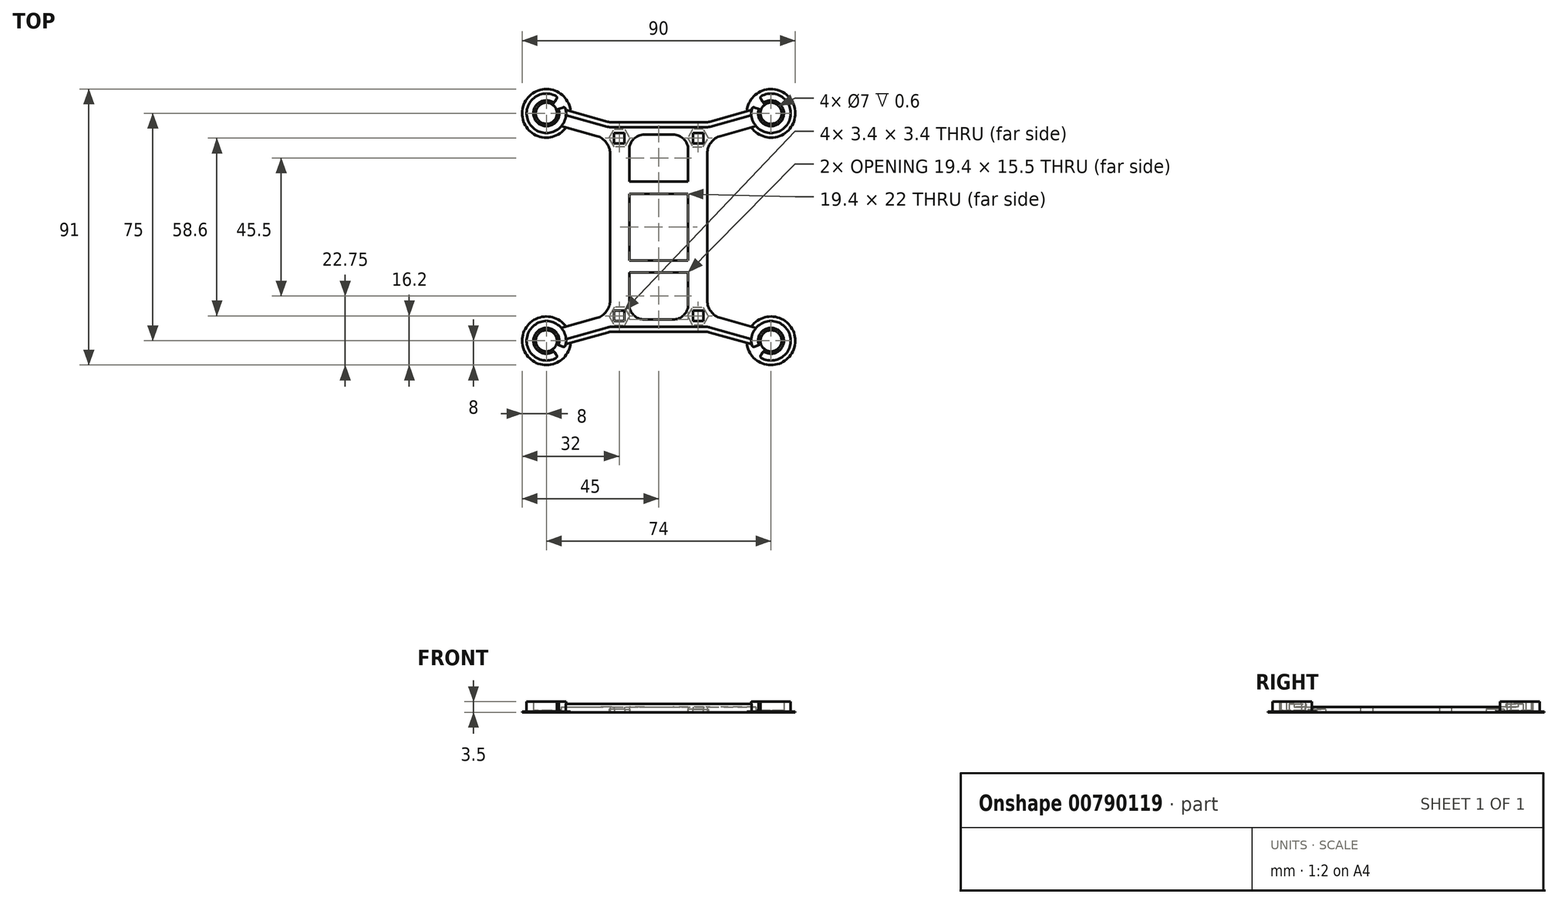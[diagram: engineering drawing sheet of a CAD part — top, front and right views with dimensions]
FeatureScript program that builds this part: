
annotation { "Feature Type Name" : "Feature", "Feature Type Description" : "" }
export const myFeature = defineFeature(function(context is Context, id is Id, definition is map)
    precondition{}
    {
        {
            var Q0;
            Q0=qCreatedBy(makeId("Top.planeOp"),FACE);
            var sketch = newSketch(context, id + "F0", { "sketchPlane" : qUnion([Q0])});
            skCircle(sketch, "E0", {"center": v(-37, 37.5) * mm, "radius": 32.5 * mm, "construction": true});
            skCircle(sketch, "E1.MirrorC", {"center": v(37, 37.5) * mm, "radius": 32.5 * mm, "construction": true});
            skCircle(sketch, "E2.MirrorC", {"center": v(37, -37.5) * mm, "radius": 32.5 * mm, "construction": true});
            skCircle(sketch, "E3.MirrorC", {"center": v(-37, -37.5) * mm, "radius": 32.5 * mm, "construction": true});
            skLineSegment(sketch, "E4.bottom", {"start": v(-37, 37.5) * mm, "end": v(37, 37.5) * mm, "construction": true});
            skLineSegment(sketch, "E4.top", {"start": v(-37, -37.5) * mm, "end": v(37, -37.5) * mm, "construction": true});
            skLineSegment(sketch, "E4.left", {"start": v(-37, 37.5) * mm, "end": v(-37, -37.5) * mm, "construction": true});
            skLineSegment(sketch, "E4.right", {"start": v(37, 37.5) * mm, "end": v(37, -37.5) * mm, "construction": true});
            skLineSegment(sketch, "E5", {"start": v(-37, 37.5) * mm, "end": v(0, 0) * mm, "construction": true});
            skCircle(sketch, "E6", {"center": v(-37, 37.5) * mm, "radius": 3.5 * mm});
            skCircle(sketch, "E7.MirrorC", {"center": v(37, 37.5) * mm, "radius": 3.5 * mm});
            skCircle(sketch, "E8.MirrorC", {"center": v(37, -37.5) * mm, "radius": 3.5 * mm});
            skCircle(sketch, "E9.MirrorC", {"center": v(-37, -37.5) * mm, "radius": 3.5 * mm});
            skArc(sketch, "E10", {"start": v(-30.59, 38.57) * mm, "mid": v(-43.26, 39.25) * mm, "end": v(-32.07, 33.27) * mm});
            skArc(sketch, "E11.MirrorC", {"start": v(30.59, 38.57) * mm, "mid": v(43.26, 39.25) * mm, "end": v(32.07, 33.27) * mm});
            skArc(sketch, "E12.MirrorC", {"start": v(-30.59, -38.57) * mm, "mid": v(-43.26, -39.25) * mm, "end": v(-32.07, -33.27) * mm});
            skArc(sketch, "E13.MirrorC", {"start": v(30.59, -38.57) * mm, "mid": v(43.26, -39.25) * mm, "end": v(32.07, -33.27) * mm});
            skLineSegment(sketch, "E14.bottom", {"start": v(-16, 34.5) * mm, "end": v(16, 34.5) * mm});
            skLineSegment(sketch, "E14.top", {"start": v(-16, -34.5) * mm, "end": v(16, -34.5) * mm});
            skLineSegment(sketch, "E14.left", {"start": v(-16, 28.8) * mm, "end": v(-16, -28.8) * mm});
            skLineSegment(sketch, "E14.right", {"start": v(16, 28.8) * mm, "end": v(16, -28.8) * mm});
            skLineSegment(sketch, "E15", {"start": v(-30.59, 38.57) * mm, "end": v(-16, 34.5) * mm});
            skLineSegment(sketch, "E16", {"start": v(-32.07, 33.27) * mm, "end": v(-16, 28.8) * mm});
            skLineSegment(sketch, "E17", {"start": v(-37, 37.5) * mm, "end": v(-17.81, 32.15) * mm, "construction": true});
            skLineSegment(sketch, "E18.MirrorCS", {"start": v(30.59, 38.57) * mm, "end": v(16, 34.5) * mm});
            skLineSegment(sketch, "E19.MirrorCS", {"start": v(32.07, 33.27) * mm, "end": v(16, 28.8) * mm});
            skLineSegment(sketch, "E20.MirrorCS", {"start": v(-30.59, -38.57) * mm, "end": v(-16, -34.5) * mm});
            skLineSegment(sketch, "E21.MirrorCS", {"start": v(-32.07, -33.27) * mm, "end": v(-16, -28.8) * mm});
            skLineSegment(sketch, "E22.MirrorCS", {"start": v(30.59, -38.57) * mm, "end": v(16, -34.5) * mm});
            skLineSegment(sketch, "E23.MirrorCS", {"start": v(32.07, -33.27) * mm, "end": v(16, -28.8) * mm});
            skCircle(sketch, "E24", {"center": v(-13, 29.3) * mm, "radius": 1.7 * mm, "construction": true});
            skLineSegment(sketch, "E25.bottom", {"start": v(-14.7, 27.6) * mm, "end": v(-11.3, 27.6) * mm});
            skLineSegment(sketch, "E25.top", {"start": v(-14.7, 31) * mm, "end": v(-11.3, 31) * mm});
            skLineSegment(sketch, "E25.left", {"start": v(-14.7, 27.6) * mm, "end": v(-14.7, 31) * mm});
            skLineSegment(sketch, "E25.right", {"start": v(-11.3, 27.6) * mm, "end": v(-11.3, 31) * mm});
            skCircle(sketch, "E26.MirrorC", {"center": v(13, 29.3) * mm, "radius": 1.7 * mm, "construction": true});
            skLineSegment(sketch, "E27.MirrorCS", {"start": v(14.7, 27.6) * mm, "end": v(14.7, 31) * mm});
            skLineSegment(sketch, "E28.MirrorCS", {"start": v(14.7, 27.6) * mm, "end": v(11.3, 27.6) * mm});
            skLineSegment(sketch, "E29.MirrorCS", {"start": v(14.7, 31) * mm, "end": v(11.3, 31) * mm});
            skLineSegment(sketch, "E30.MirrorCS", {"start": v(11.3, 27.6) * mm, "end": v(11.3, 31) * mm});
            skLineSegment(sketch, "E31.MirrorCS", {"start": v(-11.3, -27.6) * mm, "end": v(-11.3, -31) * mm});
            skLineSegment(sketch, "E32.MirrorCS", {"start": v(-14.7, -27.6) * mm, "end": v(-11.3, -27.6) * mm});
            skPoint(sketch, "E33.MirrorP", {"position": v(-13, -29.3) * mm});
            skLineSegment(sketch, "E34.MirrorCS", {"start": v(-14.7, -27.6) * mm, "end": v(-14.7, -31) * mm});
            skLineSegment(sketch, "E35.MirrorCS", {"start": v(-14.7, -31) * mm, "end": v(-11.3, -31) * mm});
            skCircle(sketch, "E36.MirrorC", {"center": v(-13, -29.3) * mm, "radius": 1.7 * mm, "construction": true});
            skLineSegment(sketch, "E37.MirrorCS", {"start": v(11.3, -27.6) * mm, "end": v(11.3, -31) * mm});
            skLineSegment(sketch, "E38.MirrorCS", {"start": v(14.7, -27.6) * mm, "end": v(14.7, -31) * mm});
            skPoint(sketch, "E39.MirrorP", {"position": v(13, -29.3) * mm});
            skLineSegment(sketch, "E40.MirrorCS", {"start": v(14.7, -27.6) * mm, "end": v(11.3, -27.6) * mm});
            skLineSegment(sketch, "E41.MirrorCS", {"start": v(14.7, -31) * mm, "end": v(11.3, -31) * mm});
            skCircle(sketch, "E42.MirrorC", {"center": v(13, -29.3) * mm, "radius": 1.7 * mm, "construction": true});
            skLineSegment(sketch, "E43.bottom", {"start": v(-9.7, 30.5) * mm, "end": v(9.7, 30.5) * mm});
            skLineSegment(sketch, "E43.top", {"start": v(-9.7, -30.5) * mm, "end": v(9.7, -30.5) * mm});
            skLineSegment(sketch, "E43.left", {"start": v(-9.7, 30.5) * mm, "end": v(-9.7, 15) * mm});
            skLineSegment(sketch, "E43.right", {"start": v(9.7, 30.5) * mm, "end": v(9.7, 15) * mm});
            skPoint(sketch, "E43.middle", {"position": v(0, 0) * mm});
            skLineSegment(sketch, "E44", {"start": v(-9.7, 15) * mm, "end": v(9.7, 15) * mm});
            skLineSegment(sketch, "E45", {"start": v(-9.7, 11) * mm, "end": v(9.7, 11) * mm});
            skLineSegment(sketch, "E46.trimOffspring", {"start": v(-9.7, 11) * mm, "end": v(-9.7, -11) * mm});
            skLineSegment(sketch, "E47.trimOffspring", {"start": v(9.7, 11) * mm, "end": v(9.7, -11) * mm});
            skLineSegment(sketch, "E48.MirrorCS", {"start": v(-9.7, -15) * mm, "end": v(9.7, -15) * mm});
            skLineSegment(sketch, "E49.MirrorCS", {"start": v(-9.7, -11) * mm, "end": v(9.7, -11) * mm});
            skLineSegment(sketch, "E50.trimOffspring", {"start": v(-9.7, -15) * mm, "end": v(-9.7, -30.5) * mm});
            skLineSegment(sketch, "E51.trimOffspring", {"start": v(9.7, -15) * mm, "end": v(9.7, -30.5) * mm});
            skSolve(sketch);
        }
        {
            var Q0;
            Q0=makeQuery(id+"F0.imprint","IMPRINT",FACE,{"disambiguationData":[TD([[makeQuery(id+"F0.imprint","IMPRINT",EDGE,{"derivedFrom":sQuery(id+"F0.wireOp",EDGE,"E6")}),-1.0]])]});
            extrude(context, id + "F1", {"entities" : qUnion([Q0]), "depth" : 1.8 * mm, "offsetDistance" : 25 * mm});
        }
        {
            var Q0;
            {var subQ0=sQuery(id+"F0.wireOp",EDGE,"E19.MirrorCS");var subQ1=sQuery(id+"F0.wireOp",EDGE,"E18.MirrorCS");var subQ2=sQuery(id+"F0.wireOp",EDGE,"E15");var subQ3=sQuery(id+"F0.wireOp",EDGE,"E14.right");var subQ4=sQuery(id+"F0.wireOp",EDGE,"E14.left");var subQ5=sQuery(id+"F0.wireOp",EDGE,"E21.MirrorCS");var subQ6=sQuery(id+"F0.wireOp",EDGE,"E8.MirrorC");var subQ7=sQuery(id+"F0.wireOp",EDGE,"E20.MirrorCS");var subQ8=sQuery(id+"F0.wireOp",EDGE,"E7.MirrorC");var subQ9=sQuery(id+"F0.wireOp",EDGE,"E22.MirrorCS");var subQ10=sQuery(id+"F0.wireOp",EDGE,"E9.MirrorC");var subQ11=sQuery(id+"F0.wireOp",EDGE,"E16");var subQ12=sQuery(id+"F0.wireOp",EDGE,"E6");var subQ13=sQuery(id+"F0.wireOp",EDGE,"E23.MirrorCS");var subQ14=sQuery(id+"F0.wireOp",EDGE,"E10");var subQ15=sQuery(id+"F0.wireOp",EDGE,"VeSnMQNN-z8bE-hv4o-3KPX-j8t92ye6yIPs.bottom");var subQ16=sQuery(id+"F0.wireOp",EDGE,"E11.MirrorC");var subQ17=sQuery(id+"F0.wireOp",EDGE,"E14.bottom");var subQ18=sQuery(id+"F0.wireOp",EDGE,"VeSnMQNN-z8bE-hv4o-3KPX-j8t92ye6yIPs.top");var subQ19=sQuery(id+"F0.wireOp",EDGE,"E12.MirrorC");var subQ20=sQuery(id+"F0.wireOp",EDGE,"E14.top");var subQ21=sQuery(id+"F0.wireOp",EDGE,"E13.MirrorC");var subQ22=sQuery(id+"F0.wireOp",EDGE,"VeSnMQNN-z8bE-hv4o-3KPX-j8t92ye6yIPs.left");var subQ23=sQuery(id+"F0.wireOp",EDGE,"VeSnMQNN-z8bE-hv4o-3KPX-j8t92ye6yIPs.right");var subQ24=sQuery(id+"F0.wireOp",EDGE,"ZSD4Ky20-EYxc-FWoI-gEsr-kIySItuAO5Qx.bottom");var subQ25=sQuery(id+"F0.wireOp",EDGE,"ZSD4Ky20-EYxc-FWoI-gEsr-kIySItuAO5Qx.top");var subQ26=sQuery(id+"F0.wireOp",EDGE,"ZSD4Ky20-EYxc-FWoI-gEsr-kIySItuAO5Qx.left");var subQ27=sQuery(id+"F0.wireOp",EDGE,"ZSD4Ky20-EYxc-FWoI-gEsr-kIySItuAO5Qx.right");var subQ28=sQuery(id+"F0.wireOp",EDGE,"E24");var subQ29=sQuery(id+"F0.wireOp",EDGE,"537b51fb-d3ba-4b39-a2e6-75db477870da0.MirrorC");var subQ30=sQuery(id+"F0.wireOp",EDGE,"21eaaf30-b72e-4287-80b9-b6d08cc284520.MirrorC");var subQ31=sQuery(id+"F0.wireOp",EDGE,"c3999cdf-1692-4670-8b73-b56c3265b7b80.MirrorC");var subQ32=sQuery(id+"F0.wireOp",EDGE,"LB6rmxyj-JH5l-yOl6-IWSN-3rPoN5P4rQFK");var subQ33=sQuery(id+"F0.wireOp",EDGE,"e03a44ee-9eac-46e1-b4e1-07f127c7162c0.MirrorC");Q0=makeQuery(id+"FtGyGyGmqmCUee5_1.boolean.opBoolean","SPLIT",FACE,{"disambiguationData":[TD([makeQuery(id+"F1.opExtrude","SWEPT_FACE",FACE,{"disambiguationData":[OSD([subQ12])]})])],"derivedFrom":makeQuery(id+"F1.opExtrude","CAP_FACE",FACE,{"disambiguationData":[OSD([subQ12,subQ8,subQ6,subQ10,subQ14,subQ16,subQ19,subQ21,sQuery(id+"F0.wireOp",EDGE,"OEuxbBry-tFTV-eClO-UwLZ-WerC2cCVn3jZ.bottom"),sQuery(id+"F0.wireOp",EDGE,"OEuxbBry-tFTV-eClO-UwLZ-WerC2cCVn3jZ.top"),sQuery(id+"F0.wireOp",EDGE,"OEuxbBry-tFTV-eClO-UwLZ-WerC2cCVn3jZ.left"),sQuery(id+"F0.wireOp",EDGE,"OEuxbBry-tFTV-eClO-UwLZ-WerC2cCVn3jZ.right"),sQuery(id+"F0.wireOp",EDGE,"4cshLyuP-iW0M-89KP-jrIE-Nz9LNLNT9eLc.top"),sQuery(id+"F0.wireOp",EDGE,"4cshLyuP-iW0M-89KP-jrIE-Nz9LNLNT9eLc.left"),sQuery(id+"F0.wireOp",EDGE,"4cshLyuP-iW0M-89KP-jrIE-Nz9LNLNT9eLc.right"),sQuery(id+"F0.wireOp",EDGE,"067346d7-7eba-45e3-80ca-d68583bf3d61.trimOffspring"),subQ17,subQ20,subQ4,subQ3,subQ2,subQ11,subQ1,subQ0,subQ7,subQ5,subQ9,subQ13,subQ15,subQ18,subQ22,subQ23,subQ24,subQ25,subQ26,subQ27,subQ28,subQ29,subQ30,subQ31,subQ32,subQ33])],"isStart":false})});}
            var sketch = newSketch(context, id + "F2", { "sketchPlane" : qUnion([Q0])});
            skCircle(sketch, "E52", {"center": v(-37, 37.5) * mm, "radius": 4.25 * mm});
            skCircle(sketch, "E53", {"center": v(-37, 37.5) * mm, "radius": 6.5 * mm});
            skCircle(sketch, "E54.MirrorC", {"center": v(37, 37.5) * mm, "radius": 4.25 * mm});
            skCircle(sketch, "E55.MirrorC", {"center": v(37, 37.5) * mm, "radius": 6.5 * mm});
            skCircle(sketch, "E56.MirrorC", {"center": v(-37, -37.5) * mm, "radius": 6.5 * mm});
            skCircle(sketch, "E57.MirrorC", {"center": v(-37, -37.5) * mm, "radius": 4.25 * mm});
            skCircle(sketch, "E58.MirrorC", {"center": v(37, -37.5) * mm, "radius": 6.5 * mm});
            skCircle(sketch, "E59.MirrorC", {"center": v(37, -37.5) * mm, "radius": 4.25 * mm});
            skSolve(sketch);
        }
        {
            var Q0;
            Q0=qSketchRegion(id+"F2",true);
            extrude(context, id + "F3", {"entities" : qUnion([Q0]), "operationType" : NewBodyOperationType.ADD, "depth" : 1.7 * mm, "offsetDistance" : 25 * mm});
        }
        {
            var Q0;
            Q0=makeQuery(id+"F1.opExtrude","SWEPT_EDGE",EDGE,{"disambiguationData":[OSD([sQuery(id+"F0.wireOp",EDGE,"E14.left"),sQuery(id+"F0.wireOp",EDGE,"E16")])]});
            var Q1;
            Q1=makeQuery(id+"F1.opExtrude","SWEPT_EDGE",EDGE,{"disambiguationData":[OSD([sQuery(id+"F0.wireOp",EDGE,"E14.left"),sQuery(id+"F0.wireOp",EDGE,"E21.MirrorCS")])]});
            var Q2;
            Q2=makeQuery(id+"F1.opExtrude","SWEPT_EDGE",EDGE,{"disambiguationData":[OSD([sQuery(id+"F0.wireOp",EDGE,"E14.bottom"),sQuery(id+"F0.wireOp",EDGE,"E18.MirrorCS")])]});
            var Q3;
            Q3=makeQuery(id+"F1.opExtrude","SWEPT_EDGE",EDGE,{"disambiguationData":[OSD([sQuery(id+"F0.wireOp",EDGE,"E14.bottom"),sQuery(id+"F0.wireOp",EDGE,"E15")])]});
            var Q4;
            Q4=makeQuery(id+"F1.opExtrude","SWEPT_EDGE",EDGE,{"disambiguationData":[OSD([sQuery(id+"F0.wireOp",EDGE,"E14.right"),sQuery(id+"F0.wireOp",EDGE,"E19.MirrorCS")])]});
            var Q5;
            Q5=makeQuery(id+"F1.opExtrude","SWEPT_EDGE",EDGE,{"disambiguationData":[OSD([sQuery(id+"F0.wireOp",EDGE,"E14.right"),sQuery(id+"F0.wireOp",EDGE,"E23.MirrorCS")])]});
            var Q6;
            Q6=makeQuery(id+"F1.opExtrude","SWEPT_EDGE",EDGE,{"disambiguationData":[OSD([sQuery(id+"F0.wireOp",EDGE,"E14.top"),sQuery(id+"F0.wireOp",EDGE,"E22.MirrorCS")])]});
            var Q7;
            Q7=makeQuery(id+"F1.opExtrude","SWEPT_EDGE",EDGE,{"disambiguationData":[OSD([sQuery(id+"F0.wireOp",EDGE,"E14.top"),sQuery(id+"F0.wireOp",EDGE,"E20.MirrorCS")])]});
            fillet(context, id + "F4", {"entities" : qUnion([Q0, Q1, Q2, Q3, Q4, Q5, Q6, Q7]), "radius" : 6 * mm, "tangentPropagation" : true, "allowEdgeOverflow" : false});
        }
        {
            var Q0;
            {var subQ0=sQuery(id+"F0.wireOp",EDGE,"OEuxbBry-tFTV-eClO-UwLZ-WerC2cCVn3jZ.top");Q0=makeQuery(id+"FT0I1PGMpONH9qH_1.boolean.opBoolean","MERGE",FACE,{"derivedFrom":[makeQuery(id+"FXMYLW3zVfJuBRl_1.boolean.opBoolean","MERGE",FACE,{"derivedFrom":[makeQuery(id+"F1.opExtrude","CAP_FACE",FACE,{"disambiguationData":[OSD([sQuery(id+"F0.wireOp",EDGE,"E6"),sQuery(id+"F0.wireOp",EDGE,"E7.MirrorC"),sQuery(id+"F0.wireOp",EDGE,"E8.MirrorC"),sQuery(id+"F0.wireOp",EDGE,"E9.MirrorC"),sQuery(id+"F0.wireOp",EDGE,"E10"),sQuery(id+"F0.wireOp",EDGE,"E11.MirrorC"),sQuery(id+"F0.wireOp",EDGE,"E12.MirrorC"),sQuery(id+"F0.wireOp",EDGE,"E13.MirrorC"),sQuery(id+"F0.wireOp",EDGE,"OEuxbBry-tFTV-eClO-UwLZ-WerC2cCVn3jZ.bottom"),subQ0,sQuery(id+"F0.wireOp",EDGE,"OEuxbBry-tFTV-eClO-UwLZ-WerC2cCVn3jZ.left"),sQuery(id+"F0.wireOp",EDGE,"OEuxbBry-tFTV-eClO-UwLZ-WerC2cCVn3jZ.right"),sQuery(id+"F0.wireOp",EDGE,"4cshLyuP-iW0M-89KP-jrIE-Nz9LNLNT9eLc.top"),sQuery(id+"F0.wireOp",EDGE,"4cshLyuP-iW0M-89KP-jrIE-Nz9LNLNT9eLc.left"),sQuery(id+"F0.wireOp",EDGE,"4cshLyuP-iW0M-89KP-jrIE-Nz9LNLNT9eLc.right"),sQuery(id+"F0.wireOp",EDGE,"067346d7-7eba-45e3-80ca-d68583bf3d61.trimOffspring"),sQuery(id+"F0.wireOp",EDGE,"E14.bottom"),sQuery(id+"F0.wireOp",EDGE,"E14.top"),sQuery(id+"F0.wireOp",EDGE,"E14.left"),sQuery(id+"F0.wireOp",EDGE,"E14.right"),sQuery(id+"F0.wireOp",EDGE,"E15"),sQuery(id+"F0.wireOp",EDGE,"E16"),sQuery(id+"F0.wireOp",EDGE,"E18.MirrorCS"),sQuery(id+"F0.wireOp",EDGE,"E19.MirrorCS"),sQuery(id+"F0.wireOp",EDGE,"E20.MirrorCS"),sQuery(id+"F0.wireOp",EDGE,"E21.MirrorCS"),sQuery(id+"F0.wireOp",EDGE,"E22.MirrorCS"),sQuery(id+"F0.wireOp",EDGE,"E23.MirrorCS"),sQuery(id+"F0.wireOp",EDGE,"VeSnMQNN-z8bE-hv4o-3KPX-j8t92ye6yIPs.bottom"),sQuery(id+"F0.wireOp",EDGE,"VeSnMQNN-z8bE-hv4o-3KPX-j8t92ye6yIPs.top"),sQuery(id+"F0.wireOp",EDGE,"VeSnMQNN-z8bE-hv4o-3KPX-j8t92ye6yIPs.left"),sQuery(id+"F0.wireOp",EDGE,"VeSnMQNN-z8bE-hv4o-3KPX-j8t92ye6yIPs.right"),sQuery(id+"F0.wireOp",EDGE,"ZSD4Ky20-EYxc-FWoI-gEsr-kIySItuAO5Qx.bottom"),sQuery(id+"F0.wireOp",EDGE,"ZSD4Ky20-EYxc-FWoI-gEsr-kIySItuAO5Qx.top"),sQuery(id+"F0.wireOp",EDGE,"ZSD4Ky20-EYxc-FWoI-gEsr-kIySItuAO5Qx.left"),sQuery(id+"F0.wireOp",EDGE,"ZSD4Ky20-EYxc-FWoI-gEsr-kIySItuAO5Qx.right"),sQuery(id+"F0.wireOp",EDGE,"E24"),sQuery(id+"F0.wireOp",EDGE,"537b51fb-d3ba-4b39-a2e6-75db477870da0.MirrorC"),sQuery(id+"F0.wireOp",EDGE,"21eaaf30-b72e-4287-80b9-b6d08cc284520.MirrorC"),sQuery(id+"F0.wireOp",EDGE,"c3999cdf-1692-4670-8b73-b56c3265b7b80.MirrorC")])],"isStart":true}),makeQuery(id+"FXMYLW3zVfJuBRl_1.opExtrude","SWEPT_FACE",FACE,{"disambiguationData":[OSD([subQ0]),TDD([makeQuery(id+"F1.opExtrude","CAP_EDGE",EDGE,{"disambiguationData":[OSD([subQ0])],"isStart":true})])]})]}),makeQuery(id+"FT0I1PGMpONH9qH_1.opExtrude","CAP_FACE",FACE,{"disambiguationData":[OSD([sQuery(id+"FLAkBSM6AbmlYxZ_1.wireOp",EDGE,"l3bJnFCj-M2iK-p7GR-cAED-iNeZcQrLd74v.bottom"),sQuery(id+"FLAkBSM6AbmlYxZ_1.wireOp",EDGE,"l3bJnFCj-M2iK-p7GR-cAED-iNeZcQrLd74v.top"),sQuery(id+"FLAkBSM6AbmlYxZ_1.wireOp",EDGE,"l3bJnFCj-M2iK-p7GR-cAED-iNeZcQrLd74v.left"),sQuery(id+"FLAkBSM6AbmlYxZ_1.wireOp",EDGE,"l3bJnFCj-M2iK-p7GR-cAED-iNeZcQrLd74v.right")])],"isStart":false})]});}
            var sketch = newSketch(context, id + "F5", { "sketchPlane" : qUnion([Q0])});
            skSolve(sketch);
        }
        {
            var Q0;
            Q0=makeQuery(id+"F3.opExtrude","CAP_FACE",FACE,{"disambiguationData":[OSD([sQuery(id+"F2.wireOp",EDGE,"E54.MirrorC"),sQuery(id+"F2.wireOp",EDGE,"E55.MirrorC")])],"isStart":false});
            var sketch = newSketch(context, id + "F6", { "sketchPlane" : qUnion([Q0])});
            skLineSegment(sketch, "E60", {"start": v(17.89, 51.86) * mm, "end": v(37, 37.5) * mm, "construction": true});
            skLineSegment(sketch, "E61", {"start": v(22.54, 42.6) * mm, "end": v(37, 37.5) * mm});
            skLineSegment(sketch, "E62", {"start": v(28.08, 49.97) * mm, "end": v(22.54, 42.6) * mm});
            skLineSegment(sketch, "E63", {"start": v(37, 37.5) * mm, "end": v(28.08, 49.97) * mm});
            skLineSegment(sketch, "E64.MirrorCS", {"start": v(-22.54, 42.6) * mm, "end": v(-37, 37.5) * mm});
            skLineSegment(sketch, "E65.MirrorCS", {"start": v(-28.08, 49.97) * mm, "end": v(-22.54, 42.6) * mm});
            skLineSegment(sketch, "E66.MirrorCS", {"start": v(-37, 37.5) * mm, "end": v(-28.08, 49.97) * mm});
            skLineSegment(sketch, "E67.MirrorCS", {"start": v(-17.89, 51.86) * mm, "end": v(-37, 37.5) * mm, "construction": true});
            skLineSegment(sketch, "E68.MirrorCS", {"start": v(-17.89, -51.86) * mm, "end": v(-37, -37.5) * mm, "construction": true});
            skLineSegment(sketch, "E69.MirrorCS", {"start": v(-22.54, -42.6) * mm, "end": v(-37, -37.5) * mm});
            skLineSegment(sketch, "E70.MirrorCS", {"start": v(17.89, -51.86) * mm, "end": v(37, -37.5) * mm, "construction": true});
            skLineSegment(sketch, "E71.MirrorCS", {"start": v(-37, -37.5) * mm, "end": v(-28.08, -49.97) * mm});
            skLineSegment(sketch, "E72.MirrorCS", {"start": v(37, -37.5) * mm, "end": v(28.08, -49.97) * mm});
            skLineSegment(sketch, "E73.MirrorCS", {"start": v(22.54, -42.6) * mm, "end": v(37, -37.5) * mm});
            skLineSegment(sketch, "E74.MirrorCS", {"start": v(28.08, -49.97) * mm, "end": v(22.54, -42.6) * mm});
            skLineSegment(sketch, "E75.MirrorCS", {"start": v(-28.08, -49.97) * mm, "end": v(-22.54, -42.6) * mm});
            skSolve(sketch);
        }
        {
            var Q0;
            Q0 = qSketchRegion(id + "F6", true);
            extrude(context, id + "F7", {"entities" : qUnion([Q0]), "operationType" : NewBodyOperationType.REMOVE, "oppositeDirection" : true, "depth" : 25 * mm, "offsetDistance" : 25 * mm});
        }
        {
            var Q0;
            Q0=makeQuery(id+"F7.boolean.opBoolean","INTERSECT",EDGE,{"derivedFrom":[makeQuery(id+"F3.boolean.opBoolean","MERGE",FACE,{"derivedFrom":[makeQuery(id+"F1.opExtrude","SWEPT_FACE",FACE,{"disambiguationData":[OSD([sQuery(id+"F0.wireOp",EDGE,"E13.MirrorC")])]}),makeQuery(id+"F3.opExtrude","SWEPT_FACE",FACE,{"disambiguationData":[OSD([sQuery(id+"F2.wireOp",EDGE,"E58.MirrorC")])]})]}),makeQuery(id+"F7.opExtrude","SWEPT_FACE",FACE,{"disambiguationData":[OSD([sQuery(id+"F6.wireOp",EDGE,"E72.MirrorCS")])]})]});
            var Q1;
            Q1=makeQuery(id+"F7.boolean.opBoolean","INTERSECT",EDGE,{"derivedFrom":[makeQuery(id+"F3.boolean.opBoolean","MERGE",FACE,{"derivedFrom":[makeQuery(id+"F1.opExtrude","SWEPT_FACE",FACE,{"disambiguationData":[OSD([sQuery(id+"F0.wireOp",EDGE,"E13.MirrorC")])]}),makeQuery(id+"F3.opExtrude","SWEPT_FACE",FACE,{"disambiguationData":[OSD([sQuery(id+"F2.wireOp",EDGE,"E58.MirrorC")])]})]}),makeQuery(id+"F7.opExtrude","SWEPT_FACE",FACE,{"disambiguationData":[OSD([sQuery(id+"F6.wireOp",EDGE,"E73.MirrorCS")])]})]});
            var Q2;
            Q2=makeQuery(id+"F7.boolean.opBoolean","INTERSECT",EDGE,{"derivedFrom":[makeQuery(id+"F3.opExtrude","SWEPT_FACE",FACE,{"disambiguationData":[OSD([sQuery(id+"F2.wireOp",EDGE,"E59.MirrorC")])]}),makeQuery(id+"F7.opExtrude","SWEPT_FACE",FACE,{"disambiguationData":[OSD([sQuery(id+"F6.wireOp",EDGE,"E73.MirrorCS")])]})]});
            var Q3;
            Q3=makeQuery(id+"F7.boolean.opBoolean","INTERSECT",EDGE,{"derivedFrom":[makeQuery(id+"F1.opExtrude","SWEPT_FACE",FACE,{"disambiguationData":[OSD([sQuery(id+"F0.wireOp",EDGE,"E8.MirrorC")])]}),makeQuery(id+"F7.opExtrude","SWEPT_FACE",FACE,{"disambiguationData":[OSD([sQuery(id+"F6.wireOp",EDGE,"E73.MirrorCS")])]})]});
            var Q4;
            Q4=makeQuery(id+"F7.boolean.opBoolean","INTERSECT",EDGE,{"derivedFrom":[makeQuery(id+"F1.opExtrude","SWEPT_FACE",FACE,{"disambiguationData":[OSD([sQuery(id+"F0.wireOp",EDGE,"E8.MirrorC")])]}),makeQuery(id+"F7.opExtrude","SWEPT_FACE",FACE,{"disambiguationData":[OSD([sQuery(id+"F6.wireOp",EDGE,"E72.MirrorCS")])]})]});
            var Q5;
            Q5=makeQuery(id+"F7.boolean.opBoolean","INTERSECT",EDGE,{"derivedFrom":[makeQuery(id+"F3.opExtrude","SWEPT_FACE",FACE,{"disambiguationData":[OSD([sQuery(id+"F2.wireOp",EDGE,"E59.MirrorC")])]}),makeQuery(id+"F7.opExtrude","SWEPT_FACE",FACE,{"disambiguationData":[OSD([sQuery(id+"F6.wireOp",EDGE,"E72.MirrorCS")])]})]});
            var Q6;
            Q6=makeQuery(id+"F7.boolean.opBoolean","INTERSECT",EDGE,{"derivedFrom":[makeQuery(id+"F3.boolean.opBoolean","MERGE",FACE,{"derivedFrom":[makeQuery(id+"F1.opExtrude","SWEPT_FACE",FACE,{"disambiguationData":[OSD([sQuery(id+"F0.wireOp",EDGE,"E12.MirrorC")])]}),makeQuery(id+"F3.opExtrude","SWEPT_FACE",FACE,{"disambiguationData":[OSD([sQuery(id+"F2.wireOp",EDGE,"E56.MirrorC")])]})]}),makeQuery(id+"F7.opExtrude","SWEPT_FACE",FACE,{"disambiguationData":[OSD([sQuery(id+"F6.wireOp",EDGE,"E71.MirrorCS")])]})]});
            var Q7;
            Q7=makeQuery(id+"F7.boolean.opBoolean","INTERSECT",EDGE,{"derivedFrom":[makeQuery(id+"F3.boolean.opBoolean","MERGE",FACE,{"derivedFrom":[makeQuery(id+"F1.opExtrude","SWEPT_FACE",FACE,{"disambiguationData":[OSD([sQuery(id+"F0.wireOp",EDGE,"E12.MirrorC")])]}),makeQuery(id+"F3.opExtrude","SWEPT_FACE",FACE,{"disambiguationData":[OSD([sQuery(id+"F2.wireOp",EDGE,"E56.MirrorC")])]})]}),makeQuery(id+"F7.opExtrude","SWEPT_FACE",FACE,{"disambiguationData":[OSD([sQuery(id+"F6.wireOp",EDGE,"E69.MirrorCS")])]})]});
            var Q8;
            Q8=makeQuery(id+"F7.boolean.opBoolean","INTERSECT",EDGE,{"derivedFrom":[makeQuery(id+"F3.opExtrude","SWEPT_FACE",FACE,{"disambiguationData":[OSD([sQuery(id+"F2.wireOp",EDGE,"E57.MirrorC")])]}),makeQuery(id+"F7.opExtrude","SWEPT_FACE",FACE,{"disambiguationData":[OSD([sQuery(id+"F6.wireOp",EDGE,"E71.MirrorCS")])]})]});
            var Q9;
            Q9=makeQuery(id+"F7.boolean.opBoolean","INTERSECT",EDGE,{"derivedFrom":[makeQuery(id+"F1.opExtrude","SWEPT_FACE",FACE,{"disambiguationData":[OSD([sQuery(id+"F0.wireOp",EDGE,"E9.MirrorC")])]}),makeQuery(id+"F7.opExtrude","SWEPT_FACE",FACE,{"disambiguationData":[OSD([sQuery(id+"F6.wireOp",EDGE,"E71.MirrorCS")])]})]});
            var Q10;
            Q10=makeQuery(id+"F7.boolean.opBoolean","INTERSECT",EDGE,{"derivedFrom":[makeQuery(id+"F3.opExtrude","SWEPT_FACE",FACE,{"disambiguationData":[OSD([sQuery(id+"F2.wireOp",EDGE,"E57.MirrorC")])]}),makeQuery(id+"F7.opExtrude","SWEPT_FACE",FACE,{"disambiguationData":[OSD([sQuery(id+"F6.wireOp",EDGE,"E69.MirrorCS")])]})]});
            var Q11;
            Q11=makeQuery(id+"F7.boolean.opBoolean","INTERSECT",EDGE,{"derivedFrom":[makeQuery(id+"F1.opExtrude","SWEPT_FACE",FACE,{"disambiguationData":[OSD([sQuery(id+"F0.wireOp",EDGE,"E9.MirrorC")])]}),makeQuery(id+"F7.opExtrude","SWEPT_FACE",FACE,{"disambiguationData":[OSD([sQuery(id+"F6.wireOp",EDGE,"E69.MirrorCS")])]})]});
            var Q12;
            Q12=makeQuery(id+"F7.boolean.opBoolean","INTERSECT",EDGE,{"derivedFrom":[makeQuery(id+"F3.boolean.opBoolean","MERGE",FACE,{"derivedFrom":[makeQuery(id+"F1.opExtrude","SWEPT_FACE",FACE,{"disambiguationData":[OSD([sQuery(id+"F0.wireOp",EDGE,"E11.MirrorC")])]}),makeQuery(id+"F3.opExtrude","SWEPT_FACE",FACE,{"disambiguationData":[OSD([sQuery(id+"F2.wireOp",EDGE,"E55.MirrorC")])]})]}),makeQuery(id+"F7.opExtrude","SWEPT_FACE",FACE,{"disambiguationData":[OSD([sQuery(id+"F6.wireOp",EDGE,"E63")])]})]});
            var Q13;
            Q13=makeQuery(id+"F7.boolean.opBoolean","INTERSECT",EDGE,{"derivedFrom":[makeQuery(id+"F3.boolean.opBoolean","MERGE",FACE,{"derivedFrom":[makeQuery(id+"F1.opExtrude","SWEPT_FACE",FACE,{"disambiguationData":[OSD([sQuery(id+"F0.wireOp",EDGE,"E11.MirrorC")])]}),makeQuery(id+"F3.opExtrude","SWEPT_FACE",FACE,{"disambiguationData":[OSD([sQuery(id+"F2.wireOp",EDGE,"E55.MirrorC")])]})]}),makeQuery(id+"F7.opExtrude","SWEPT_FACE",FACE,{"disambiguationData":[OSD([sQuery(id+"F6.wireOp",EDGE,"E61")])]})]});
            var Q14;
            Q14=makeQuery(id+"F7.boolean.opBoolean","INTERSECT",EDGE,{"derivedFrom":[makeQuery(id+"F3.opExtrude","SWEPT_FACE",FACE,{"disambiguationData":[OSD([sQuery(id+"F2.wireOp",EDGE,"E54.MirrorC")])]}),makeQuery(id+"F7.opExtrude","SWEPT_FACE",FACE,{"disambiguationData":[OSD([sQuery(id+"F6.wireOp",EDGE,"E61")])]})]});
            var Q15;
            Q15=makeQuery(id+"F7.boolean.opBoolean","INTERSECT",EDGE,{"derivedFrom":[makeQuery(id+"F1.opExtrude","SWEPT_FACE",FACE,{"disambiguationData":[OSD([sQuery(id+"F0.wireOp",EDGE,"E7.MirrorC")])]}),makeQuery(id+"F7.opExtrude","SWEPT_FACE",FACE,{"disambiguationData":[OSD([sQuery(id+"F6.wireOp",EDGE,"E61")])]})]});
            var Q16;
            Q16=makeQuery(id+"F7.boolean.opBoolean","INTERSECT",EDGE,{"derivedFrom":[makeQuery(id+"F1.opExtrude","SWEPT_FACE",FACE,{"disambiguationData":[OSD([sQuery(id+"F0.wireOp",EDGE,"E7.MirrorC")])]}),makeQuery(id+"F7.opExtrude","SWEPT_FACE",FACE,{"disambiguationData":[OSD([sQuery(id+"F6.wireOp",EDGE,"E63")])]})]});
            var Q17;
            Q17=makeQuery(id+"F7.boolean.opBoolean","INTERSECT",EDGE,{"derivedFrom":[makeQuery(id+"F3.opExtrude","SWEPT_FACE",FACE,{"disambiguationData":[OSD([sQuery(id+"F2.wireOp",EDGE,"E54.MirrorC")])]}),makeQuery(id+"F7.opExtrude","SWEPT_FACE",FACE,{"disambiguationData":[OSD([sQuery(id+"F6.wireOp",EDGE,"E63")])]})]});
            var Q18;
            Q18=makeQuery(id+"F7.boolean.opBoolean","INTERSECT",EDGE,{"derivedFrom":[makeQuery(id+"F3.boolean.opBoolean","MERGE",FACE,{"derivedFrom":[makeQuery(id+"F1.opExtrude","SWEPT_FACE",FACE,{"disambiguationData":[OSD([sQuery(id+"F0.wireOp",EDGE,"E10")])]}),makeQuery(id+"F3.opExtrude","SWEPT_FACE",FACE,{"disambiguationData":[OSD([sQuery(id+"F2.wireOp",EDGE,"E53")])]})]}),makeQuery(id+"F7.opExtrude","SWEPT_FACE",FACE,{"disambiguationData":[OSD([sQuery(id+"F6.wireOp",EDGE,"E64.MirrorCS")])]})]});
            var Q19;
            Q19=makeQuery(id+"F7.boolean.opBoolean","INTERSECT",EDGE,{"derivedFrom":[makeQuery(id+"F3.boolean.opBoolean","MERGE",FACE,{"derivedFrom":[makeQuery(id+"F1.opExtrude","SWEPT_FACE",FACE,{"disambiguationData":[OSD([sQuery(id+"F0.wireOp",EDGE,"E10")])]}),makeQuery(id+"F3.opExtrude","SWEPT_FACE",FACE,{"disambiguationData":[OSD([sQuery(id+"F2.wireOp",EDGE,"E53")])]})]}),makeQuery(id+"F7.opExtrude","SWEPT_FACE",FACE,{"disambiguationData":[OSD([sQuery(id+"F6.wireOp",EDGE,"E66.MirrorCS")])]})]});
            var Q20;
            Q20=makeQuery(id+"F7.boolean.opBoolean","INTERSECT",EDGE,{"derivedFrom":[makeQuery(id+"F3.opExtrude","SWEPT_FACE",FACE,{"disambiguationData":[OSD([sQuery(id+"F2.wireOp",EDGE,"E52")])]}),makeQuery(id+"F7.opExtrude","SWEPT_FACE",FACE,{"disambiguationData":[OSD([sQuery(id+"F6.wireOp",EDGE,"E64.MirrorCS")])]})]});
            var Q21;
            Q21=makeQuery(id+"F7.boolean.opBoolean","INTERSECT",EDGE,{"derivedFrom":[makeQuery(id+"F1.opExtrude","SWEPT_FACE",FACE,{"disambiguationData":[OSD([sQuery(id+"F0.wireOp",EDGE,"E6")])]}),makeQuery(id+"F7.opExtrude","SWEPT_FACE",FACE,{"disambiguationData":[OSD([sQuery(id+"F6.wireOp",EDGE,"E64.MirrorCS")])]})]});
            var Q22;
            Q22=makeQuery(id+"F7.boolean.opBoolean","INTERSECT",EDGE,{"derivedFrom":[makeQuery(id+"F3.opExtrude","SWEPT_FACE",FACE,{"disambiguationData":[OSD([sQuery(id+"F2.wireOp",EDGE,"E52")])]}),makeQuery(id+"F7.opExtrude","SWEPT_FACE",FACE,{"disambiguationData":[OSD([sQuery(id+"F6.wireOp",EDGE,"E66.MirrorCS")])]})]});
            var Q23;
            Q23=makeQuery(id+"F7.boolean.opBoolean","INTERSECT",EDGE,{"derivedFrom":[makeQuery(id+"F1.opExtrude","SWEPT_FACE",FACE,{"disambiguationData":[OSD([sQuery(id+"F0.wireOp",EDGE,"E6")])]}),makeQuery(id+"F7.opExtrude","SWEPT_FACE",FACE,{"disambiguationData":[OSD([sQuery(id+"F6.wireOp",EDGE,"E66.MirrorCS")])]})]});
            fillet(context, id + "F8", {"entities" : qUnion([Q0, Q1, Q2, Q3, Q4, Q5, Q6, Q7, Q8, Q9, Q10, Q11, Q12, Q13, Q14, Q15, Q16, Q17, Q18, Q19, Q20, Q21, Q22, Q23]), "radius" : 0.62 * mm, "tangentPropagation" : true, "allowEdgeOverflow" : false});
        }
        {
            var Q0;
            {var subQ0=sQuery(id+"F0.wireOp",EDGE,"E8.MirrorC");var subQ1=sQuery(id+"F0.wireOp",EDGE,"OEuxbBry-tFTV-eClO-UwLZ-WerC2cCVn3jZ.top");Q0=makeQuery(id+"F3.boolean.opBoolean","SPLIT",FACE,{"disambiguationData":[TD([makeQuery(id+"F1.opExtrude","SWEPT_FACE",FACE,{"disambiguationData":[OSD([subQ0])]})])],"derivedFrom":makeQuery(id+"FXMYLW3zVfJuBRl_1.boolean.opBoolean","MERGE",FACE,{"derivedFrom":[makeQuery(id+"F1.opExtrude","CAP_FACE",FACE,{"disambiguationData":[OSD([sQuery(id+"F0.wireOp",EDGE,"E6"),sQuery(id+"F0.wireOp",EDGE,"E7.MirrorC"),subQ0,sQuery(id+"F0.wireOp",EDGE,"E9.MirrorC"),sQuery(id+"F0.wireOp",EDGE,"E10"),sQuery(id+"F0.wireOp",EDGE,"E11.MirrorC"),sQuery(id+"F0.wireOp",EDGE,"E12.MirrorC"),sQuery(id+"F0.wireOp",EDGE,"E13.MirrorC"),sQuery(id+"F0.wireOp",EDGE,"OEuxbBry-tFTV-eClO-UwLZ-WerC2cCVn3jZ.bottom"),subQ1,sQuery(id+"F0.wireOp",EDGE,"OEuxbBry-tFTV-eClO-UwLZ-WerC2cCVn3jZ.left"),sQuery(id+"F0.wireOp",EDGE,"OEuxbBry-tFTV-eClO-UwLZ-WerC2cCVn3jZ.right"),sQuery(id+"F0.wireOp",EDGE,"4cshLyuP-iW0M-89KP-jrIE-Nz9LNLNT9eLc.top"),sQuery(id+"F0.wireOp",EDGE,"4cshLyuP-iW0M-89KP-jrIE-Nz9LNLNT9eLc.left"),sQuery(id+"F0.wireOp",EDGE,"4cshLyuP-iW0M-89KP-jrIE-Nz9LNLNT9eLc.right"),sQuery(id+"F0.wireOp",EDGE,"067346d7-7eba-45e3-80ca-d68583bf3d61.trimOffspring"),sQuery(id+"F0.wireOp",EDGE,"E14.bottom"),sQuery(id+"F0.wireOp",EDGE,"E14.top"),sQuery(id+"F0.wireOp",EDGE,"E14.left"),sQuery(id+"F0.wireOp",EDGE,"E14.right"),sQuery(id+"F0.wireOp",EDGE,"E15"),sQuery(id+"F0.wireOp",EDGE,"E16"),sQuery(id+"F0.wireOp",EDGE,"E18.MirrorCS"),sQuery(id+"F0.wireOp",EDGE,"E19.MirrorCS"),sQuery(id+"F0.wireOp",EDGE,"E20.MirrorCS"),sQuery(id+"F0.wireOp",EDGE,"E21.MirrorCS"),sQuery(id+"F0.wireOp",EDGE,"E22.MirrorCS"),sQuery(id+"F0.wireOp",EDGE,"E23.MirrorCS"),sQuery(id+"F0.wireOp",EDGE,"VeSnMQNN-z8bE-hv4o-3KPX-j8t92ye6yIPs.bottom"),sQuery(id+"F0.wireOp",EDGE,"VeSnMQNN-z8bE-hv4o-3KPX-j8t92ye6yIPs.top"),sQuery(id+"F0.wireOp",EDGE,"VeSnMQNN-z8bE-hv4o-3KPX-j8t92ye6yIPs.left"),sQuery(id+"F0.wireOp",EDGE,"VeSnMQNN-z8bE-hv4o-3KPX-j8t92ye6yIPs.right"),sQuery(id+"F0.wireOp",EDGE,"ZSD4Ky20-EYxc-FWoI-gEsr-kIySItuAO5Qx.bottom"),sQuery(id+"F0.wireOp",EDGE,"ZSD4Ky20-EYxc-FWoI-gEsr-kIySItuAO5Qx.top"),sQuery(id+"F0.wireOp",EDGE,"ZSD4Ky20-EYxc-FWoI-gEsr-kIySItuAO5Qx.left"),sQuery(id+"F0.wireOp",EDGE,"ZSD4Ky20-EYxc-FWoI-gEsr-kIySItuAO5Qx.right"),sQuery(id+"F0.wireOp",EDGE,"E24"),sQuery(id+"F0.wireOp",EDGE,"537b51fb-d3ba-4b39-a2e6-75db477870da0.MirrorC"),sQuery(id+"F0.wireOp",EDGE,"21eaaf30-b72e-4287-80b9-b6d08cc284520.MirrorC"),sQuery(id+"F0.wireOp",EDGE,"c3999cdf-1692-4670-8b73-b56c3265b7b80.MirrorC")])],"isStart":false}),makeQuery(id+"FXMYLW3zVfJuBRl_1.opExtrude","SWEPT_FACE",FACE,{"disambiguationData":[OSD([subQ1]),TDD([makeQuery(id+"F1.opExtrude","CAP_EDGE",EDGE,{"disambiguationData":[OSD([subQ1])],"isStart":false})])]})]})});}
            var Q1;
            {var subQ0=sQuery(id+"F0.wireOp",EDGE,"E9.MirrorC");var subQ1=sQuery(id+"F0.wireOp",EDGE,"OEuxbBry-tFTV-eClO-UwLZ-WerC2cCVn3jZ.top");Q1=makeQuery(id+"F3.boolean.opBoolean","SPLIT",FACE,{"disambiguationData":[TD([makeQuery(id+"F1.opExtrude","SWEPT_FACE",FACE,{"disambiguationData":[OSD([subQ0])]})])],"derivedFrom":makeQuery(id+"FXMYLW3zVfJuBRl_1.boolean.opBoolean","MERGE",FACE,{"derivedFrom":[makeQuery(id+"F1.opExtrude","CAP_FACE",FACE,{"disambiguationData":[OSD([sQuery(id+"F0.wireOp",EDGE,"E6"),sQuery(id+"F0.wireOp",EDGE,"E7.MirrorC"),sQuery(id+"F0.wireOp",EDGE,"E8.MirrorC"),subQ0,sQuery(id+"F0.wireOp",EDGE,"E10"),sQuery(id+"F0.wireOp",EDGE,"E11.MirrorC"),sQuery(id+"F0.wireOp",EDGE,"E12.MirrorC"),sQuery(id+"F0.wireOp",EDGE,"E13.MirrorC"),sQuery(id+"F0.wireOp",EDGE,"OEuxbBry-tFTV-eClO-UwLZ-WerC2cCVn3jZ.bottom"),subQ1,sQuery(id+"F0.wireOp",EDGE,"OEuxbBry-tFTV-eClO-UwLZ-WerC2cCVn3jZ.left"),sQuery(id+"F0.wireOp",EDGE,"OEuxbBry-tFTV-eClO-UwLZ-WerC2cCVn3jZ.right"),sQuery(id+"F0.wireOp",EDGE,"4cshLyuP-iW0M-89KP-jrIE-Nz9LNLNT9eLc.top"),sQuery(id+"F0.wireOp",EDGE,"4cshLyuP-iW0M-89KP-jrIE-Nz9LNLNT9eLc.left"),sQuery(id+"F0.wireOp",EDGE,"4cshLyuP-iW0M-89KP-jrIE-Nz9LNLNT9eLc.right"),sQuery(id+"F0.wireOp",EDGE,"067346d7-7eba-45e3-80ca-d68583bf3d61.trimOffspring"),sQuery(id+"F0.wireOp",EDGE,"E14.bottom"),sQuery(id+"F0.wireOp",EDGE,"E14.top"),sQuery(id+"F0.wireOp",EDGE,"E14.left"),sQuery(id+"F0.wireOp",EDGE,"E14.right"),sQuery(id+"F0.wireOp",EDGE,"E15"),sQuery(id+"F0.wireOp",EDGE,"E16"),sQuery(id+"F0.wireOp",EDGE,"E18.MirrorCS"),sQuery(id+"F0.wireOp",EDGE,"E19.MirrorCS"),sQuery(id+"F0.wireOp",EDGE,"E20.MirrorCS"),sQuery(id+"F0.wireOp",EDGE,"E21.MirrorCS"),sQuery(id+"F0.wireOp",EDGE,"E22.MirrorCS"),sQuery(id+"F0.wireOp",EDGE,"E23.MirrorCS"),sQuery(id+"F0.wireOp",EDGE,"VeSnMQNN-z8bE-hv4o-3KPX-j8t92ye6yIPs.bottom"),sQuery(id+"F0.wireOp",EDGE,"VeSnMQNN-z8bE-hv4o-3KPX-j8t92ye6yIPs.top"),sQuery(id+"F0.wireOp",EDGE,"VeSnMQNN-z8bE-hv4o-3KPX-j8t92ye6yIPs.left"),sQuery(id+"F0.wireOp",EDGE,"VeSnMQNN-z8bE-hv4o-3KPX-j8t92ye6yIPs.right"),sQuery(id+"F0.wireOp",EDGE,"ZSD4Ky20-EYxc-FWoI-gEsr-kIySItuAO5Qx.bottom"),sQuery(id+"F0.wireOp",EDGE,"ZSD4Ky20-EYxc-FWoI-gEsr-kIySItuAO5Qx.top"),sQuery(id+"F0.wireOp",EDGE,"ZSD4Ky20-EYxc-FWoI-gEsr-kIySItuAO5Qx.left"),sQuery(id+"F0.wireOp",EDGE,"ZSD4Ky20-EYxc-FWoI-gEsr-kIySItuAO5Qx.right"),sQuery(id+"F0.wireOp",EDGE,"E24"),sQuery(id+"F0.wireOp",EDGE,"537b51fb-d3ba-4b39-a2e6-75db477870da0.MirrorC"),sQuery(id+"F0.wireOp",EDGE,"21eaaf30-b72e-4287-80b9-b6d08cc284520.MirrorC"),sQuery(id+"F0.wireOp",EDGE,"c3999cdf-1692-4670-8b73-b56c3265b7b80.MirrorC")])],"isStart":false}),makeQuery(id+"FXMYLW3zVfJuBRl_1.opExtrude","SWEPT_FACE",FACE,{"disambiguationData":[OSD([subQ1]),TDD([makeQuery(id+"F1.opExtrude","CAP_EDGE",EDGE,{"disambiguationData":[OSD([subQ1])],"isStart":false})])]})]})});}
            var Q2;
            {var subQ0=sQuery(id+"F0.wireOp",EDGE,"E6");var subQ1=sQuery(id+"F0.wireOp",EDGE,"OEuxbBry-tFTV-eClO-UwLZ-WerC2cCVn3jZ.top");Q2=makeQuery(id+"F3.boolean.opBoolean","SPLIT",FACE,{"disambiguationData":[TD([makeQuery(id+"F1.opExtrude","SWEPT_FACE",FACE,{"disambiguationData":[OSD([subQ0])]})])],"derivedFrom":makeQuery(id+"FXMYLW3zVfJuBRl_1.boolean.opBoolean","MERGE",FACE,{"derivedFrom":[makeQuery(id+"F1.opExtrude","CAP_FACE",FACE,{"disambiguationData":[OSD([subQ0,sQuery(id+"F0.wireOp",EDGE,"E7.MirrorC"),sQuery(id+"F0.wireOp",EDGE,"E8.MirrorC"),sQuery(id+"F0.wireOp",EDGE,"E9.MirrorC"),sQuery(id+"F0.wireOp",EDGE,"E10"),sQuery(id+"F0.wireOp",EDGE,"E11.MirrorC"),sQuery(id+"F0.wireOp",EDGE,"E12.MirrorC"),sQuery(id+"F0.wireOp",EDGE,"E13.MirrorC"),sQuery(id+"F0.wireOp",EDGE,"OEuxbBry-tFTV-eClO-UwLZ-WerC2cCVn3jZ.bottom"),subQ1,sQuery(id+"F0.wireOp",EDGE,"OEuxbBry-tFTV-eClO-UwLZ-WerC2cCVn3jZ.left"),sQuery(id+"F0.wireOp",EDGE,"OEuxbBry-tFTV-eClO-UwLZ-WerC2cCVn3jZ.right"),sQuery(id+"F0.wireOp",EDGE,"4cshLyuP-iW0M-89KP-jrIE-Nz9LNLNT9eLc.top"),sQuery(id+"F0.wireOp",EDGE,"4cshLyuP-iW0M-89KP-jrIE-Nz9LNLNT9eLc.left"),sQuery(id+"F0.wireOp",EDGE,"4cshLyuP-iW0M-89KP-jrIE-Nz9LNLNT9eLc.right"),sQuery(id+"F0.wireOp",EDGE,"067346d7-7eba-45e3-80ca-d68583bf3d61.trimOffspring"),sQuery(id+"F0.wireOp",EDGE,"E14.bottom"),sQuery(id+"F0.wireOp",EDGE,"E14.top"),sQuery(id+"F0.wireOp",EDGE,"E14.left"),sQuery(id+"F0.wireOp",EDGE,"E14.right"),sQuery(id+"F0.wireOp",EDGE,"E15"),sQuery(id+"F0.wireOp",EDGE,"E16"),sQuery(id+"F0.wireOp",EDGE,"E18.MirrorCS"),sQuery(id+"F0.wireOp",EDGE,"E19.MirrorCS"),sQuery(id+"F0.wireOp",EDGE,"E20.MirrorCS"),sQuery(id+"F0.wireOp",EDGE,"E21.MirrorCS"),sQuery(id+"F0.wireOp",EDGE,"E22.MirrorCS"),sQuery(id+"F0.wireOp",EDGE,"E23.MirrorCS"),sQuery(id+"F0.wireOp",EDGE,"VeSnMQNN-z8bE-hv4o-3KPX-j8t92ye6yIPs.bottom"),sQuery(id+"F0.wireOp",EDGE,"VeSnMQNN-z8bE-hv4o-3KPX-j8t92ye6yIPs.top"),sQuery(id+"F0.wireOp",EDGE,"VeSnMQNN-z8bE-hv4o-3KPX-j8t92ye6yIPs.left"),sQuery(id+"F0.wireOp",EDGE,"VeSnMQNN-z8bE-hv4o-3KPX-j8t92ye6yIPs.right"),sQuery(id+"F0.wireOp",EDGE,"ZSD4Ky20-EYxc-FWoI-gEsr-kIySItuAO5Qx.bottom"),sQuery(id+"F0.wireOp",EDGE,"ZSD4Ky20-EYxc-FWoI-gEsr-kIySItuAO5Qx.top"),sQuery(id+"F0.wireOp",EDGE,"ZSD4Ky20-EYxc-FWoI-gEsr-kIySItuAO5Qx.left"),sQuery(id+"F0.wireOp",EDGE,"ZSD4Ky20-EYxc-FWoI-gEsr-kIySItuAO5Qx.right"),sQuery(id+"F0.wireOp",EDGE,"E24"),sQuery(id+"F0.wireOp",EDGE,"537b51fb-d3ba-4b39-a2e6-75db477870da0.MirrorC"),sQuery(id+"F0.wireOp",EDGE,"21eaaf30-b72e-4287-80b9-b6d08cc284520.MirrorC"),sQuery(id+"F0.wireOp",EDGE,"c3999cdf-1692-4670-8b73-b56c3265b7b80.MirrorC")])],"isStart":false}),makeQuery(id+"FXMYLW3zVfJuBRl_1.opExtrude","SWEPT_FACE",FACE,{"disambiguationData":[OSD([subQ1]),TDD([makeQuery(id+"F1.opExtrude","CAP_EDGE",EDGE,{"disambiguationData":[OSD([subQ1])],"isStart":false})])]})]})});}
            var Q3;
            {var subQ0=sQuery(id+"F0.wireOp",EDGE,"E7.MirrorC");var subQ1=sQuery(id+"F0.wireOp",EDGE,"OEuxbBry-tFTV-eClO-UwLZ-WerC2cCVn3jZ.top");Q3=makeQuery(id+"F3.boolean.opBoolean","SPLIT",FACE,{"disambiguationData":[TD([makeQuery(id+"F1.opExtrude","SWEPT_FACE",FACE,{"disambiguationData":[OSD([subQ0])]})])],"derivedFrom":makeQuery(id+"FXMYLW3zVfJuBRl_1.boolean.opBoolean","MERGE",FACE,{"derivedFrom":[makeQuery(id+"F1.opExtrude","CAP_FACE",FACE,{"disambiguationData":[OSD([sQuery(id+"F0.wireOp",EDGE,"E6"),subQ0,sQuery(id+"F0.wireOp",EDGE,"E8.MirrorC"),sQuery(id+"F0.wireOp",EDGE,"E9.MirrorC"),sQuery(id+"F0.wireOp",EDGE,"E10"),sQuery(id+"F0.wireOp",EDGE,"E11.MirrorC"),sQuery(id+"F0.wireOp",EDGE,"E12.MirrorC"),sQuery(id+"F0.wireOp",EDGE,"E13.MirrorC"),sQuery(id+"F0.wireOp",EDGE,"OEuxbBry-tFTV-eClO-UwLZ-WerC2cCVn3jZ.bottom"),subQ1,sQuery(id+"F0.wireOp",EDGE,"OEuxbBry-tFTV-eClO-UwLZ-WerC2cCVn3jZ.left"),sQuery(id+"F0.wireOp",EDGE,"OEuxbBry-tFTV-eClO-UwLZ-WerC2cCVn3jZ.right"),sQuery(id+"F0.wireOp",EDGE,"4cshLyuP-iW0M-89KP-jrIE-Nz9LNLNT9eLc.top"),sQuery(id+"F0.wireOp",EDGE,"4cshLyuP-iW0M-89KP-jrIE-Nz9LNLNT9eLc.left"),sQuery(id+"F0.wireOp",EDGE,"4cshLyuP-iW0M-89KP-jrIE-Nz9LNLNT9eLc.right"),sQuery(id+"F0.wireOp",EDGE,"067346d7-7eba-45e3-80ca-d68583bf3d61.trimOffspring"),sQuery(id+"F0.wireOp",EDGE,"E14.bottom"),sQuery(id+"F0.wireOp",EDGE,"E14.top"),sQuery(id+"F0.wireOp",EDGE,"E14.left"),sQuery(id+"F0.wireOp",EDGE,"E14.right"),sQuery(id+"F0.wireOp",EDGE,"E15"),sQuery(id+"F0.wireOp",EDGE,"E16"),sQuery(id+"F0.wireOp",EDGE,"E18.MirrorCS"),sQuery(id+"F0.wireOp",EDGE,"E19.MirrorCS"),sQuery(id+"F0.wireOp",EDGE,"E20.MirrorCS"),sQuery(id+"F0.wireOp",EDGE,"E21.MirrorCS"),sQuery(id+"F0.wireOp",EDGE,"E22.MirrorCS"),sQuery(id+"F0.wireOp",EDGE,"E23.MirrorCS"),sQuery(id+"F0.wireOp",EDGE,"VeSnMQNN-z8bE-hv4o-3KPX-j8t92ye6yIPs.bottom"),sQuery(id+"F0.wireOp",EDGE,"VeSnMQNN-z8bE-hv4o-3KPX-j8t92ye6yIPs.top"),sQuery(id+"F0.wireOp",EDGE,"VeSnMQNN-z8bE-hv4o-3KPX-j8t92ye6yIPs.left"),sQuery(id+"F0.wireOp",EDGE,"VeSnMQNN-z8bE-hv4o-3KPX-j8t92ye6yIPs.right"),sQuery(id+"F0.wireOp",EDGE,"ZSD4Ky20-EYxc-FWoI-gEsr-kIySItuAO5Qx.bottom"),sQuery(id+"F0.wireOp",EDGE,"ZSD4Ky20-EYxc-FWoI-gEsr-kIySItuAO5Qx.top"),sQuery(id+"F0.wireOp",EDGE,"ZSD4Ky20-EYxc-FWoI-gEsr-kIySItuAO5Qx.left"),sQuery(id+"F0.wireOp",EDGE,"ZSD4Ky20-EYxc-FWoI-gEsr-kIySItuAO5Qx.right"),sQuery(id+"F0.wireOp",EDGE,"E24"),sQuery(id+"F0.wireOp",EDGE,"537b51fb-d3ba-4b39-a2e6-75db477870da0.MirrorC"),sQuery(id+"F0.wireOp",EDGE,"21eaaf30-b72e-4287-80b9-b6d08cc284520.MirrorC"),sQuery(id+"F0.wireOp",EDGE,"c3999cdf-1692-4670-8b73-b56c3265b7b80.MirrorC")])],"isStart":false}),makeQuery(id+"FXMYLW3zVfJuBRl_1.opExtrude","SWEPT_FACE",FACE,{"disambiguationData":[OSD([subQ1]),TDD([makeQuery(id+"F1.opExtrude","CAP_EDGE",EDGE,{"disambiguationData":[OSD([subQ1])],"isStart":false})])]})]})});}
            extrude(context, id + "F9", {"entities" : qUnion([Q0, Q1, Q2, Q3]), "operationType" : NewBodyOperationType.REMOVE, "oppositeDirection" : true, "depth" : 1.2 * mm, "offsetDistance" : 25 * mm});
        }
        {
            var Q0;
            {var subQ41=sQuery(id+"F0.wireOp",EDGE,"E6");Q0=makeQuery(id+"F5.imprint","IMPRINT",FACE,{"disambiguationData":[TD([[makeQuery(id+"F5.imprint","IMPRINT",EDGE,{"derivedFrom":makeQuery(id+"F1.opExtrude","CAP_EDGE",EDGE,{"disambiguationData":[OSD([subQ41])],"isStart":true})}),1.0]])]});}
            var sketch = newSketch(context, id + "F10", { "sketchPlane" : qUnion([Q0])});
            skCircle(sketch, "E76", {"center": v(-37, 37.5) * mm, "radius": 8 * mm});
            skCircle(sketch, "E77", {"center": v(-37, 37.5) * mm, "radius": 3.5 * mm});
            skCircle(sketch, "E78.MirrorC", {"center": v(37, 37.5) * mm, "radius": 8 * mm});
            skCircle(sketch, "E79.MirrorC", {"center": v(37, 37.5) * mm, "radius": 3.5 * mm});
            skCircle(sketch, "E80.MirrorC", {"center": v(37, -37.5) * mm, "radius": 8 * mm});
            skCircle(sketch, "E81.MirrorC", {"center": v(-37, -37.5) * mm, "radius": 3.5 * mm});
            skCircle(sketch, "E82.MirrorC", {"center": v(-37, -37.5) * mm, "radius": 8 * mm});
            skCircle(sketch, "E83.MirrorC", {"center": v(37, -37.5) * mm, "radius": 3.5 * mm});
            skSolve(sketch);
        }
        {
            var Q0;
            Q0 = qSketchRegion(id + "F10", true);
            extrude(context, id + "F11", {"entities" : qUnion([Q0]), "operationType" : NewBodyOperationType.ADD, "oppositeDirection" : true, "depth" : 0.3 * mm, "offsetDistance" : 25 * mm});
        }
        {
            var Q0;
            Q0=makeQuery(id+"F1.opExtrude","SWEPT_EDGE",EDGE,{"disambiguationData":[OSD([sQuery(id+"F0.wireOp",EDGE,"E43.top"),sQuery(id+"F0.wireOp",EDGE,"E50.trimOffspring")])]});
            var Q1;
            Q1=makeQuery(id+"F1.opExtrude","SWEPT_EDGE",EDGE,{"disambiguationData":[OSD([sQuery(id+"F0.wireOp",EDGE,"E43.top"),sQuery(id+"F0.wireOp",EDGE,"E51.trimOffspring")])]});
            var Q2;
            Q2=makeQuery(id+"F1.opExtrude","SWEPT_EDGE",EDGE,{"disambiguationData":[OSD([sQuery(id+"F0.wireOp",EDGE,"E43.bottom"),sQuery(id+"F0.wireOp",EDGE,"E43.left")])]});
            var Q3;
            Q3=makeQuery(id+"F1.opExtrude","SWEPT_EDGE",EDGE,{"disambiguationData":[OSD([sQuery(id+"F0.wireOp",EDGE,"E43.bottom"),sQuery(id+"F0.wireOp",EDGE,"E43.right")])]});
            fillet(context, id + "F12", {"entities" : qUnion([Q0, Q1, Q2, Q3]), "radius" : 5 * mm, "tangentPropagation" : true, "allowEdgeOverflow" : false});
        }
        {
            var Q0;
            {var subQ0=sQuery(id+"F0.wireOp",EDGE,"yX43g5sE-bQKp-hv9S-kTC7-pIAoUnp0ttJZ.top");var subQ1=sQuery(id+"F0.wireOp",EDGE,"yX43g5sE-bQKp-hv9S-kTC7-pIAoUnp0ttJZ.bottom");var subQ2=sQuery(id+"F0.wireOp",EDGE,"c3999cdf-1692-4670-8b73-b56c3265b7b80.MirrorC");var subQ3=sQuery(id+"F0.wireOp",EDGE,"21eaaf30-b72e-4287-80b9-b6d08cc284520.MirrorC");var subQ4=sQuery(id+"F0.wireOp",EDGE,"537b51fb-d3ba-4b39-a2e6-75db477870da0.MirrorC");var subQ5=sQuery(id+"F0.wireOp",EDGE,"E24");var subQ6=sQuery(id+"F0.wireOp",EDGE,"E23.MirrorCS");var subQ7=sQuery(id+"F0.wireOp",EDGE,"E22.MirrorCS");var subQ8=sQuery(id+"F0.wireOp",EDGE,"E21.MirrorCS");var subQ9=sQuery(id+"F0.wireOp",EDGE,"E20.MirrorCS");var subQ10=sQuery(id+"F0.wireOp",EDGE,"E19.MirrorCS");var subQ11=sQuery(id+"F0.wireOp",EDGE,"E18.MirrorCS");var subQ12=sQuery(id+"F0.wireOp",EDGE,"E13.MirrorC");var subQ13=sQuery(id+"F0.wireOp",EDGE,"E12.MirrorC");var subQ14=sQuery(id+"F0.wireOp",EDGE,"E11.MirrorC");var subQ15=sQuery(id+"F0.wireOp",EDGE,"E10");var subQ16=sQuery(id+"F0.wireOp",EDGE,"E14.bottom");var subQ17=sQuery(id+"F0.wireOp",EDGE,"E14.top");var subQ18=sQuery(id+"F0.wireOp",EDGE,"E14.left");var subQ19=sQuery(id+"F0.wireOp",EDGE,"E14.right");var subQ20=sQuery(id+"F0.wireOp",EDGE,"E15");var subQ21=sQuery(id+"F0.wireOp",EDGE,"E16");var subQ22=sQuery(id+"F0.wireOp",EDGE,"yX43g5sE-bQKp-hv9S-kTC7-pIAoUnp0ttJZ.left");var subQ23=sQuery(id+"F0.wireOp",EDGE,"yX43g5sE-bQKp-hv9S-kTC7-pIAoUnp0ttJZ.right");var subQ24=sQuery(id+"F0.wireOp",EDGE,"KF2gMbaP-NVOR-toOF-rTCB-IYUSVCf0NuqR");var subQ25=sQuery(id+"F0.wireOp",EDGE,"TVKdiwv4-wd8y-0Geu-1LhS-G8mtIZRfUu8W");var subQ26=sQuery(id+"F0.wireOp",EDGE,"d1050f7c-ce23-4751-9650-23b99bc6fdfd.trimOffspring");var subQ27=sQuery(id+"F0.wireOp",EDGE,"95d2c982-ae4f-42f3-9ad4-9e78db09f566.trimOffspring");Q0=makeQuery(id+"F3.boolean.opBoolean","SPLIT",FACE,{"disambiguationData":[TD([makeQuery(id+"F1.opExtrude","SWEPT_FACE",FACE,{"disambiguationData":[OSD([subQ15])]})])],"derivedFrom":makeQuery(id+"F1.opExtrude","CAP_FACE",FACE,{"disambiguationData":[OSD([sQuery(id+"F0.wireOp",EDGE,"E6"),sQuery(id+"F0.wireOp",EDGE,"E7.MirrorC"),sQuery(id+"F0.wireOp",EDGE,"E8.MirrorC"),sQuery(id+"F0.wireOp",EDGE,"E9.MirrorC"),subQ15,subQ14,subQ13,subQ12,subQ16,subQ17,subQ18,subQ19,subQ20,subQ21,subQ11,subQ10,subQ9,subQ8,subQ7,subQ6,subQ5,subQ4,subQ3,subQ2,subQ1,subQ0,subQ22,subQ23,subQ24,subQ25,subQ26,subQ27])],"isStart":false})});}
            var sketch = newSketch(context, id + "F13", { "sketchPlane" : qUnion([Q0])});
            skLineSegment(sketch, "E84.0", {"start": v(-30.59, -38.57) * mm, "end": v(-16.8, -34.72) * mm});
            skArc(sketch, "E85.0", {"start": v(-16.8, -34.72) * mm, "mid": v(-16, -34.56) * mm, "end": v(-15.18, -34.5) * mm});
            skLineSegment(sketch, "E86.0", {"start": v(-15.18, -34.5) * mm, "end": v(15.18, -34.5) * mm});
            skArc(sketch, "E87.0", {"start": v(15.18, -34.5) * mm, "mid": v(16, -34.56) * mm, "end": v(16.8, -34.72) * mm});
            skLineSegment(sketch, "E88.0", {"start": v(30.59, -38.57) * mm, "end": v(16.8, -34.72) * mm});
            skLineSegment(sketch, "E89", {"start": v(-30.53, -36.89) * mm, "end": v(-16.88, -33.08) * mm});
            skLineSegment(sketch, "E90", {"start": v(-15.53, -32.9) * mm, "end": v(15.53, -32.9) * mm});
            skLineSegment(sketch, "E91", {"start": v(16.88, -33.08) * mm, "end": v(30.53, -36.89) * mm});
            skPoint(sketch, "E92.visualSharp", {"position": v(-16.22, -32.9) * mm});
            skArc(sketch, "E92.filletArc", {"start": v(-15.53, -32.9) * mm, "mid": v(-16.21, -32.95) * mm, "end": v(-16.88, -33.08) * mm});
            skPoint(sketch, "E93.visualSharp", {"position": v(16.22, -32.9) * mm});
            skArc(sketch, "E93.filletArc", {"start": v(16.88, -33.08) * mm, "mid": v(16.21, -32.95) * mm, "end": v(15.53, -32.9) * mm});
            skArc(sketch, "E94.MirrorCS", {"start": v(15.18, 34.5) * mm, "mid": v(16, 34.56) * mm, "end": v(16.8, 34.72) * mm});
            skArc(sketch, "E95.MirrorCS", {"start": v(16.88, 33.08) * mm, "mid": v(16.21, 32.95) * mm, "end": v(15.53, 32.9) * mm});
            skArc(sketch, "E96.MirrorCS", {"start": v(-16.8, 34.72) * mm, "mid": v(-16, 34.56) * mm, "end": v(-15.18, 34.5) * mm});
            skArc(sketch, "E97.MirrorCS", {"start": v(-15.53, 32.9) * mm, "mid": v(-16.21, 32.95) * mm, "end": v(-16.88, 33.08) * mm});
            skPoint(sketch, "E98.MirrorP", {"position": v(-16.22, 32.9) * mm});
            skPoint(sketch, "E99.MirrorP", {"position": v(16.22, 32.9) * mm});
            skLineSegment(sketch, "E100.MirrorCS", {"start": v(-15.18, 34.5) * mm, "end": v(15.18, 34.5) * mm});
            skLineSegment(sketch, "E101.MirrorCS", {"start": v(-30.59, 38.57) * mm, "end": v(-16.8, 34.72) * mm});
            skLineSegment(sketch, "E102.MirrorCS", {"start": v(16.88, 33.08) * mm, "end": v(30.53, 36.89) * mm});
            skLineSegment(sketch, "E103.MirrorCS", {"start": v(-30.53, 36.89) * mm, "end": v(-16.88, 33.08) * mm});
            skLineSegment(sketch, "E104.MirrorCS", {"start": v(30.59, 38.57) * mm, "end": v(16.8, 34.72) * mm});
            skLineSegment(sketch, "E105.MirrorCS", {"start": v(-15.53, 32.9) * mm, "end": v(15.53, 32.9) * mm});
            skSolve(sketch);
        }
        {
            var Q0;
            Q0=makeQuery(id+"F13.imprint","IMPRINT",FACE,{"disambiguationData":[TD([[makeQuery(id+"F13.imprint","IMPRINT",EDGE,{"derivedFrom":sQuery(id+"F13.wireOp",EDGE,"E94.MirrorCS")}),1.0]])]});
            var Q1;
            {var subQ3=sQuery(id+"F13.wireOp",EDGE,"E84.0");Q1=makeQuery(id+"F13.imprint","IMPRINT",FACE,{"disambiguationData":[TD([[makeQuery(id+"F13.imprint","IMPRINT",EDGE,{"derivedFrom":subQ3}),1.0]])]});}
            extrude(context, id + "F14", {"entities" : qUnion([Q0, Q1]), "operationType" : NewBodyOperationType.ADD, "depth" : 1 * mm, "offsetDistance" : 25 * mm});
        }
        {
            var Q0;
            {var subQ31=sQuery(id+"F0.wireOp",EDGE,"E6");Q0=makeQuery(id+"F5.imprint","IMPRINT",FACE,{"disambiguationData":[TD([[makeQuery(id+"F5.imprint","IMPRINT",EDGE,{"derivedFrom":makeQuery(id+"F1.opExtrude","CAP_EDGE",EDGE,{"disambiguationData":[OSD([subQ31])],"isStart":true})}),1.0]])]});}
            var sketch = newSketch(context, id + "F15", { "sketchPlane" : qUnion([Q0])});
            skCircle(sketch, "E106.cCircle", {"center": v(12.93, -29.37) * mm, "radius": 2.95 * mm, "construction": true});
            skLineSegment(sketch, "E106.0", {"start": v(14.63, -32.32) * mm, "end": v(11.23, -32.32) * mm});
            skLineSegment(sketch, "E106.1", {"start": v(11.23, -32.32) * mm, "end": v(9.53, -29.37) * mm});
            skLineSegment(sketch, "E106.2", {"start": v(9.53, -29.37) * mm, "end": v(11.23, -26.42) * mm});
            skLineSegment(sketch, "E106.3", {"start": v(11.23, -26.42) * mm, "end": v(14.63, -26.42) * mm});
            skLineSegment(sketch, "E106.4", {"start": v(14.63, -26.42) * mm, "end": v(16.34, -29.37) * mm});
            skLineSegment(sketch, "E106.5", {"start": v(16.34, -29.37) * mm, "end": v(14.63, -32.32) * mm});
            skPoint(sketch, "E106.0.midPoint", {"position": v(12.93, -32.32) * mm});
            skLineSegment(sketch, "E107.MirrorCS", {"start": v(-14.63, -32.32) * mm, "end": v(-11.23, -32.32) * mm});
            skPoint(sketch, "E108.MirrorP", {"position": v(-12.93, -32.32) * mm});
            skLineSegment(sketch, "E109.MirrorCS", {"start": v(-14.63, -26.42) * mm, "end": v(-16.34, -29.37) * mm});
            skCircle(sketch, "E110.MirrorC", {"center": v(-12.93, -29.37) * mm, "radius": 2.95 * mm, "construction": true});
            skLineSegment(sketch, "E111.MirrorCS", {"start": v(-9.53, -29.37) * mm, "end": v(-11.23, -26.42) * mm});
            skLineSegment(sketch, "E112.MirrorCS", {"start": v(-11.23, -26.42) * mm, "end": v(-14.63, -26.42) * mm});
            skLineSegment(sketch, "E113.MirrorCS", {"start": v(-11.23, -32.32) * mm, "end": v(-9.53, -29.37) * mm});
            skLineSegment(sketch, "E114.MirrorCS", {"start": v(-16.34, -29.37) * mm, "end": v(-14.63, -32.32) * mm});
            skLineSegment(sketch, "E115.MirrorCS", {"start": v(16.34, 29.37) * mm, "end": v(14.63, 32.32) * mm});
            skLineSegment(sketch, "E116.MirrorCS", {"start": v(11.23, 32.32) * mm, "end": v(9.53, 29.37) * mm});
            skCircle(sketch, "E117.MirrorC", {"center": v(12.93, 29.37) * mm, "radius": 2.95 * mm, "construction": true});
            skLineSegment(sketch, "E118.MirrorCS", {"start": v(-16.34, 29.37) * mm, "end": v(-14.63, 32.32) * mm});
            skLineSegment(sketch, "E119.MirrorCS", {"start": v(14.63, 26.42) * mm, "end": v(16.34, 29.37) * mm});
            skLineSegment(sketch, "E120.MirrorCS", {"start": v(-11.23, 32.32) * mm, "end": v(-9.53, 29.37) * mm});
            skCircle(sketch, "E121.MirrorC", {"center": v(-12.93, 29.37) * mm, "radius": 2.95 * mm, "construction": true});
            skLineSegment(sketch, "E122.MirrorCS", {"start": v(11.23, 26.42) * mm, "end": v(14.63, 26.42) * mm});
            skLineSegment(sketch, "E123.MirrorCS", {"start": v(-11.23, 26.42) * mm, "end": v(-14.63, 26.42) * mm});
            skLineSegment(sketch, "E124.MirrorCS", {"start": v(9.53, 29.37) * mm, "end": v(11.23, 26.42) * mm});
            skLineSegment(sketch, "E125.MirrorCS", {"start": v(-14.63, 32.32) * mm, "end": v(-11.23, 32.32) * mm});
            skLineSegment(sketch, "E126.MirrorCS", {"start": v(-14.63, 26.42) * mm, "end": v(-16.34, 29.37) * mm});
            skLineSegment(sketch, "E127.MirrorCS", {"start": v(-9.53, 29.37) * mm, "end": v(-11.23, 26.42) * mm});
            skLineSegment(sketch, "E128.MirrorCS", {"start": v(14.63, 32.32) * mm, "end": v(11.23, 32.32) * mm});
            skPoint(sketch, "E129.MirrorP", {"position": v(-12.93, 32.32) * mm});
            skPoint(sketch, "E130.MirrorP", {"position": v(12.93, 32.32) * mm});
            skSolve(sketch);
        }
        {
            var Q0;
            Q0 = qSketchRegion(id + "F15", true);
            extrude(context, id + "F16", {"entities" : qUnion([Q0]), "operationType" : NewBodyOperationType.REMOVE, "oppositeDirection" : true, "depth" : 1 * mm, "offsetDistance" : 25 * mm});
        }
    });
